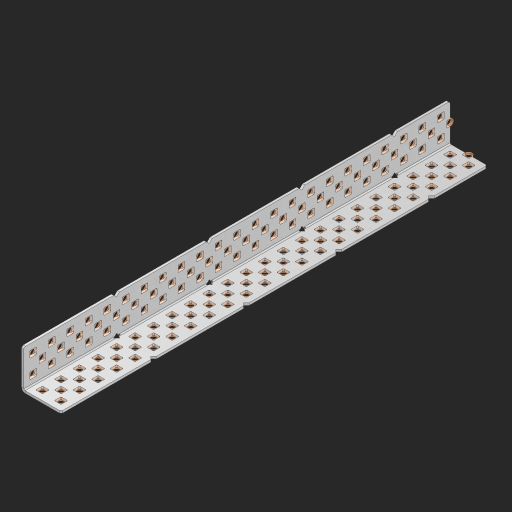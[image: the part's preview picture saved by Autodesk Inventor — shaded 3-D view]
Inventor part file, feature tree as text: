
AUTODESK INVENTOR PART (.ipt)
format: ipt  version: 2023 (Build 270158000, 158)  size: 1,702,912 bytes
history: native  units: in
note: dims shown in document units (in); Inventor stores cm internally (conversion verified against a paired STEP export)
features: other x144, extrude x136, sheet_metal_op x8, sketch x7, pattern_linear x2, mirror x1, chamfer x1
ambient origin geometry x8: Origin, YZ Plane, XZ Plane, XY Plane, X Axis, Y Axis, Z Axis, Center Point
bodies: Solid1 (feature_tree), Body (feature_tree)
feature tree (299):
  sheet_metal_op  "Flanges"
  sheet_metal_op  "Body Pattern"
  pattern_linear  "Center Pattern"  Spacing1=1.0in  [1 undecoded]
  other  "Arc Length"
  pattern_linear  "Notch Pattern"  Spacing1=0.25in  [1 undecoded]
  other  "Diagonal Plane"
  mirror  "Everything Mirrored"
  chamfer  "End Chamfer"
  sketch  "Sketch1"  dims[d0=1.0in]
  other  "Plate1"
  sketch  "Sketch2"  dims[d1=11.5in]
  other  "Plate2"
  sheet_metal_op  "Bend1"
  sheet_metal_op  "Corner1"
  sketch  "Sketch8"  dims[d2=0.0625in]
  sketch  "Sketch9"  dims[d3=0.0625in]
  other  "Srf91"
  sheet_metal_op  "Body Pattern Sketch"
  other  "Srf92"
  sketch  "Sketch13"  dims[d4=0.0312in]
  sketch  "Sketch15"  dims[d5=0.125in]
  sketch  "Sketch16"  dims[d6=0.0625in d7=1.0in d8=90.0deg d9=0.0312in d10=0.25in d11=0.0625in d12=0.0625in d49=0.182in d50=0.02in d52=0.25in d53=0.0625in d54=0.0in d55=0.172in d56=1.0in d57=0.0in d60=9.0551in d62=0.5in d63=0.7874in d65=0.5in d85=0.1473in d86=0.1782in d89=0.0625in d90=0.0in d91=0.04in d92=0.0491in d95=2.5in d96=0.04in d97=0.25in d98=45.0deg d99=0.25in d106=0.182in d107=0.02in d108=0.5in d110=0.0625in d111=0.0in d112=0.172in d113=0.5in d114=0.0in d117=0.5in d123=0.25in d125=0.25in d126=0.0491in d127=0.1473in d128=0.08in d129=0.04in d130=2.5in]
  other  "Srf786"
  other  "Srf856"
  other  "Srf857"
  other  "Srf858"
  other  "Srf859"
  other  "Srf860"
  other  "Srf861"
  other  "Srf889"
  other  "Srf890"
  other  "Srf891"
  other  "Srf1275"
  other  "Srf1276"
  other  "Srf1278"
  other  "Srf1279"
  other  "Srf1280"
  other  "Srf1281"
  other  "Srf1282"
  other  "Srf1283"
  other  "Srf1277"
  other  "Srf1285"
  other  "Srf1286"
  other  "Srf1287"
  other  "Srf1383"
  other  "Srf1384"
  other  "Srf1385"
  other  "Srf1386"
  other  "Srf1387"
  other  "Srf1388"
  other  "Srf1389"
  other  "Srf1390"
  other  "Srf1391"
  other  "Srf1392"
  other  "Srf1393"
  other  "Srf1394"
  other  "Srf1395"
  other  "Srf1396"
  other  "Srf1397"
  other  "Srf1398"
  other  "Srf1399"
  other  "Srf1400"
  other  "Srf1401"
  other  "Srf1402"
  other  "Srf1403"
  other  "Srf1404"
  other  "Srf1405"
  other  "Srf1406"
  other  "Srf1407"
  other  "Srf1408"
  other  "Srf1409"
  other  "Srf1410"
  other  "Srf1411"
  other  "Srf1412"
  other  "Srf1413"
  other  "Srf1414"
  other  "Srf1415"
  other  "Srf1416"
  other  "Srf1417"
  other  "Srf1418"
  other  "Srf1419"
  other  "Srf1420"
  other  "Srf1445"
  other  "Srf1446"
  other  "Srf1447"
  other  "Srf1448"
  other  "Srf1449"
  other  "Srf1450"
  other  "Srf1451"
  other  "Srf1452"
  other  "Srf1453"
  other  "Srf1454"
  other  "Srf1455"
  other  "Srf1456"
  other  "Srf1457"
  other  "Srf1458"
  other  "Srf1459"
  other  "Srf1460"
  other  "Srf1461"
  other  "Srf1462"
  other  "Srf1463"
  other  "Srf1475"
  other  "Srf1476"
  other  "Srf1477"
  other  "Srf1478"
  other  "Srf1479"
  other  "Srf1480"
  other  "Srf1481"
  other  "Srf1482"
  other  "Srf1483"
  other  "Srf1484"
  other  "Srf1485"
  other  "Srf1486"
  other  "Srf1487"
  other  "Srf1488"
  other  "Srf1489"
  other  "Srf1490"
  other  "Srf1491"
  other  "Srf1492"
  other  "Srf1493"
  other  "Srf1494"
  other  "Srf1495"
  other  "Srf1496"
  other  "Srf1497"
  other  "Srf1498"
  other  "Srf1499"
  other  "Srf1500"
  other  "Srf1501"
  other  "Srf1502"
  other  "Srf1503"
  other  "Srf1504"
  other  "Srf1505"
  other  "Srf1506"
  other  "Srf1507"
  other  "Srf1508"
  other  "Srf1509"
  other  "Srf1510"
  other  "Srf1511"
  other  "Srf1512"
  other  "Srf1537"
  other  "Srf1538"
  other  "Srf1539"
  other  "Srf1540"
  other  "Srf1541"
  other  "Srf1542"
  other  "Srf1543"
  other  "Srf1544"
  other  "Srf1545"
  other  "Srf1546"
  other  "Srf1547"
  other  "Srf1548"
  other  "Srf1549"
  other  "Srf1550"
  other  "Srf1551"
  other  "Srf1552"
  other  "Srf1553"
  other  "Srf1554"
  other  "Srf1555"
  sheet_metal_op  "Body Stamp"
  sheet_metal_op  "Body Circle"
  other  "Center Stamp"
  other  "Center Circle"
  sheet_metal_op  "Notch"
  extrude  "ExtrusionSrf92"  Depth=0.0625in
  extrude  "ExtrusionSrf856"  Depth=0.0625in
  extrude  "ExtrusionSrf857"  Depth=0.182in
  extrude  "ExtrusionSrf858"  Depth=0.02in
  extrude  "ExtrusionSrf859"  Depth=0.25in
  extrude  "ExtrusionSrf860"  Depth=0.0625in
  extrude  "ExtrusionSrf861"  TaperAngle=0.0deg  [1 undecoded]
  extrude  "ExtrusionSrf889"  Depth=2.5in
  extrude  "ExtrusionSrf890"  Depth=1.0in TaperAngle=0.0deg
  extrude  "ExtrusionSrf891"  Depth=2.5in
  extrude  "ExtrusionSrf1275"  Depth=0.5in
  extrude  "ExtrusionSrf1276"  Depth=2.5in
  extrude  "ExtrusionSrf1277"  Depth=2.5in
  extrude  "ExtrusionSrf1278"  Depth=0.0625in
  extrude  "ExtrusionSrf1279"  Depth=2.5in TaperAngle=0.0deg
  extrude  "ExtrusionSrf1280"  Depth=2.5in
  extrude  "ExtrusionSrf1281"  Depth=0.25in TaperAngle=45.0deg
  extrude  "ExtrusionSrf1282"  Depth=0.25in
  extrude  "ExtrusionSrf1345"  Depth=0.182in
  extrude  "ExtrusionSrf1346"  Depth=0.02in
  extrude  "ExtrusionSrf1347"  Depth=0.5in
  extrude  "ExtrusionSrf1348"  Depth=0.0625in
  extrude  "ExtrusionSrf1383"  TaperAngle=0.0deg  [1 undecoded]
  extrude  "ExtrusionSrf1384"  Depth=2.5in
  extrude  "ExtrusionSrf1385"  Depth=0.5in TaperAngle=0.0deg
  extrude  "ExtrusionSrf1386"  Depth=0.5in
  extrude  "ExtrusionSrf1387"  Depth=0.25in
  extrude  "ExtrusionSrf1388"  Depth=0.25in
  extrude  "ExtrusionSrf1389"  Depth=2.5in
  extrude  "ExtrusionSrf1390"  Depth=2.5in
  extrude  "ExtrusionSrf1391"  Depth=2.5in
  extrude  "ExtrusionSrf1392"  Depth=2.5in
  extrude  "ExtrusionSrf1393"  Depth=2.5in
  extrude  "ExtrusionSrf1394"  [1 undecoded]
  extrude  "ExtrusionSrf1395"  [1 undecoded]
  extrude  "ExtrusionSrf1396"  [1 undecoded]
  extrude  "ExtrusionSrf1397"  [1 undecoded]
  extrude  "ExtrusionSrf1398"  [1 undecoded]
  extrude  "ExtrusionSrf1399"  [1 undecoded]
  extrude  "ExtrusionSrf1400"  [1 undecoded]
  extrude  "ExtrusionSrf1401"  [1 undecoded]
  extrude  "ExtrusionSrf1402"  [1 undecoded]
  extrude  "ExtrusionSrf1403"  [1 undecoded]
  extrude  "ExtrusionSrf1404"  [1 undecoded]
  extrude  "ExtrusionSrf1405"  [1 undecoded]
  extrude  "ExtrusionSrf1406"  [1 undecoded]
  extrude  "ExtrusionSrf1407"  [1 undecoded]
  extrude  "ExtrusionSrf1408"  [1 undecoded]
  extrude  "ExtrusionSrf1409"  [1 undecoded]
  extrude  "ExtrusionSrf1410"  [1 undecoded]
  extrude  "ExtrusionSrf1411"  [1 undecoded]
  extrude  "ExtrusionSrf1412"  [1 undecoded]
  extrude  "ExtrusionSrf1413"  [1 undecoded]
  extrude  "ExtrusionSrf1414"  [1 undecoded]
  extrude  "ExtrusionSrf1415"  [1 undecoded]
  extrude  "ExtrusionSrf1416"  [1 undecoded]
  extrude  "ExtrusionSrf1417"  [1 undecoded]
  extrude  "ExtrusionSrf1418"  [1 undecoded]
  extrude  "ExtrusionSrf1419"  [1 undecoded]
  extrude  "ExtrusionSrf1420"  [1 undecoded]
  extrude  "ExtrusionSrf1445"  [1 undecoded]
  extrude  "ExtrusionSrf1446"  [1 undecoded]
  extrude  "ExtrusionSrf1447"  [1 undecoded]
  extrude  "ExtrusionSrf1448"  [1 undecoded]
  extrude  "ExtrusionSrf1449"  [1 undecoded]
  extrude  "ExtrusionSrf1450"  [1 undecoded]
  extrude  "ExtrusionSrf1451"  [1 undecoded]
  extrude  "ExtrusionSrf1452"  [1 undecoded]
  extrude  "ExtrusionSrf1453"  [1 undecoded]
  extrude  "ExtrusionSrf1454"  [1 undecoded]
  extrude  "ExtrusionSrf1455"  [1 undecoded]
  extrude  "ExtrusionSrf1456"  [1 undecoded]
  extrude  "ExtrusionSrf1457"  [1 undecoded]
  extrude  "ExtrusionSrf1458"  [1 undecoded]
  extrude  "ExtrusionSrf1459"  [1 undecoded]
  extrude  "ExtrusionSrf1460"  [1 undecoded]
  extrude  "ExtrusionSrf1461"  [1 undecoded]
  extrude  "ExtrusionSrf1462"  [1 undecoded]
  extrude  "ExtrusionSrf1463"  [1 undecoded]
  extrude  "ExtrusionSrf1475"  [1 undecoded]
  extrude  "ExtrusionSrf1476"  [1 undecoded]
  extrude  "ExtrusionSrf1477"  [1 undecoded]
  extrude  "ExtrusionSrf1478"  [1 undecoded]
  extrude  "ExtrusionSrf1479"  [1 undecoded]
  extrude  "ExtrusionSrf1480"  [1 undecoded]
  extrude  "ExtrusionSrf1481"  [1 undecoded]
  extrude  "ExtrusionSrf1482"  [1 undecoded]
  extrude  "ExtrusionSrf1483"  [1 undecoded]
  extrude  "ExtrusionSrf1484"  [1 undecoded]
  extrude  "ExtrusionSrf1485"  [1 undecoded]
  extrude  "ExtrusionSrf1486"  [1 undecoded]
  extrude  "ExtrusionSrf1487"  [1 undecoded]
  extrude  "ExtrusionSrf1488"  [1 undecoded]
  extrude  "ExtrusionSrf1489"  [1 undecoded]
  extrude  "ExtrusionSrf1490"  [1 undecoded]
  extrude  "ExtrusionSrf1491"  [1 undecoded]
  extrude  "ExtrusionSrf1492"  [1 undecoded]
  extrude  "ExtrusionSrf1493"  [1 undecoded]
  extrude  "ExtrusionSrf1494"  [1 undecoded]
  extrude  "ExtrusionSrf1495"  [1 undecoded]
  extrude  "ExtrusionSrf1496"  [1 undecoded]
  extrude  "ExtrusionSrf1497"  [1 undecoded]
  extrude  "ExtrusionSrf1498"  [1 undecoded]
  extrude  "ExtrusionSrf1499"  [1 undecoded]
  extrude  "ExtrusionSrf1500"  [1 undecoded]
  extrude  "ExtrusionSrf1501"  [1 undecoded]
  extrude  "ExtrusionSrf1502"  [1 undecoded]
  extrude  "ExtrusionSrf1503"  [1 undecoded]
  extrude  "ExtrusionSrf1504"  [1 undecoded]
  extrude  "ExtrusionSrf1505"  [1 undecoded]
  extrude  "ExtrusionSrf1506"  [1 undecoded]
  extrude  "ExtrusionSrf1507"  [1 undecoded]
  extrude  "ExtrusionSrf1508"  [1 undecoded]
  extrude  "ExtrusionSrf1509"  [1 undecoded]
  extrude  "ExtrusionSrf1510"  [1 undecoded]
  extrude  "ExtrusionSrf1511"  [1 undecoded]
  extrude  "ExtrusionSrf1512"  [1 undecoded]
  extrude  "ExtrusionSrf1537"  [1 undecoded]
  extrude  "ExtrusionSrf1538"  [1 undecoded]
  extrude  "ExtrusionSrf1539"  [1 undecoded]
  extrude  "ExtrusionSrf1540"  [1 undecoded]
  extrude  "ExtrusionSrf1541"  [1 undecoded]
  extrude  "ExtrusionSrf1542"  [1 undecoded]
  extrude  "ExtrusionSrf1543"  [1 undecoded]
  extrude  "ExtrusionSrf1544"  [1 undecoded]
  extrude  "ExtrusionSrf1545"  [1 undecoded]
  extrude  "ExtrusionSrf1546"  [1 undecoded]
  extrude  "ExtrusionSrf1547"  [1 undecoded]
  extrude  "ExtrusionSrf1548"  [1 undecoded]
  extrude  "ExtrusionSrf1549"  [1 undecoded]
  extrude  "ExtrusionSrf1550"  [1 undecoded]
  extrude  "ExtrusionSrf1551"  [1 undecoded]
  extrude  "ExtrusionSrf1552"  [1 undecoded]
  extrude  "ExtrusionSrf1553"  [1 undecoded]
  extrude  "ExtrusionSrf1554"  [1 undecoded]
  extrude  "ExtrusionSrf1555"  [1 undecoded]
note: 107 required parameter values undecoded (feature->parameter linkage not recoverable at this tier; creation-order binding heuristic only, values carry confidence <= 0.55)
